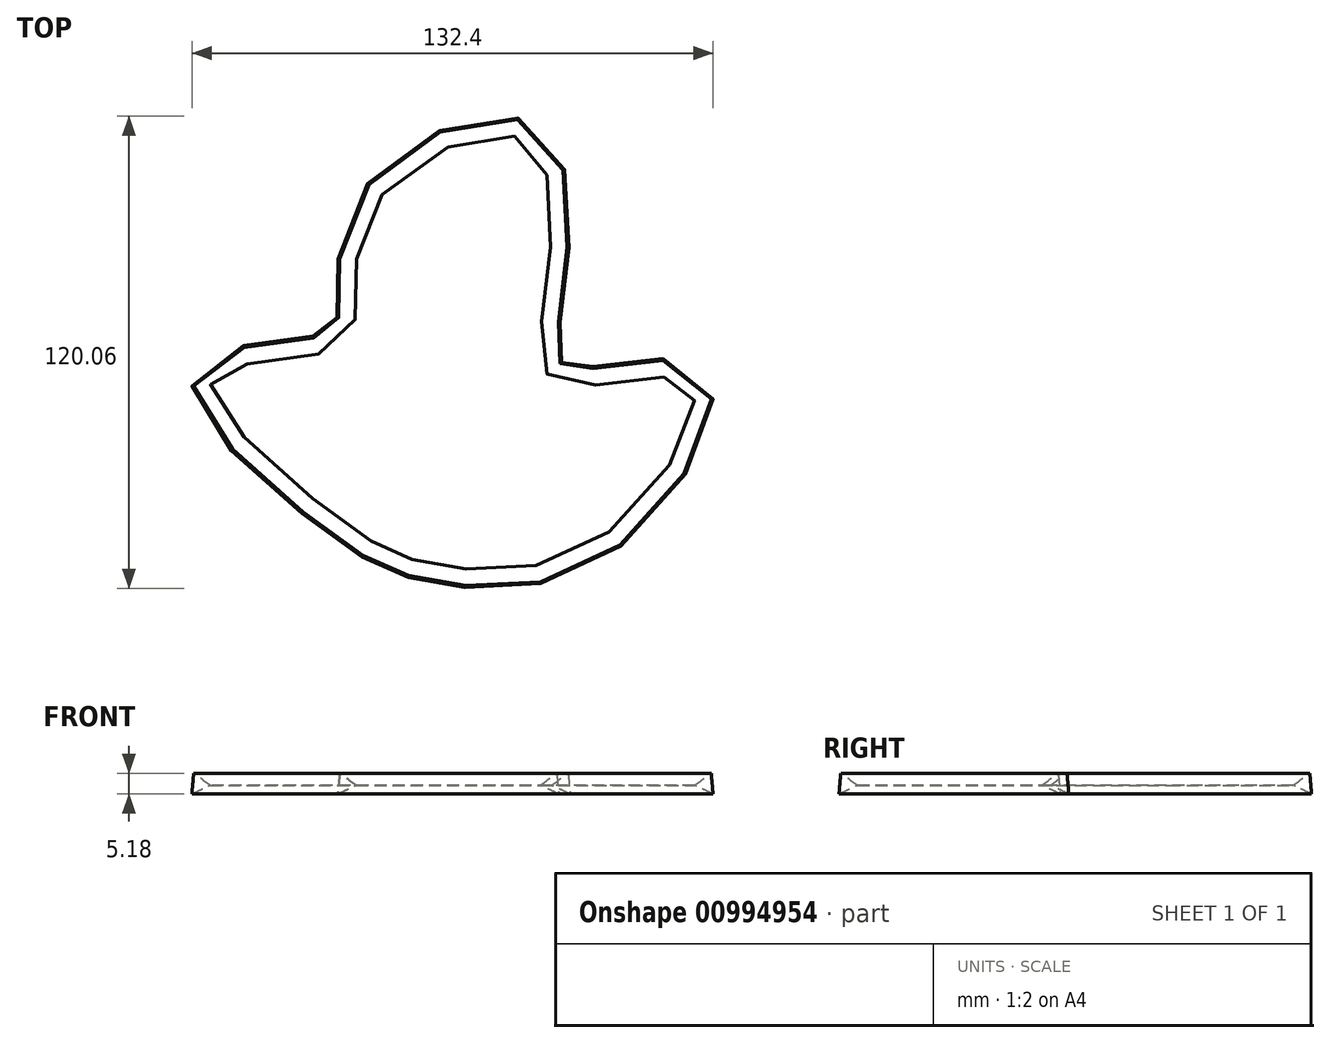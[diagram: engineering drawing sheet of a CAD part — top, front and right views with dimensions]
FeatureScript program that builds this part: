
annotation { "Feature Type Name" : "Feature", "Feature Type Description" : "" }
export const myFeature = defineFeature(function(context is Context, id is Id, definition is map)
    precondition{}
    {
        {
            var Q0;
            Q0=qCreatedBy(makeId("Front.planeOp"),FACE);
            var sketch = newSketch(context, id + "F0", { "sketchPlane" : qUnion([Q0])});
            skCircle(sketch, "E0.cCircle", {"center": v(-5.22, 0) * mm, "radius": 1.5 * mm, "construction": true});
            skLineSegment(sketch, "E0.0", {"start": v(-2.23, -0.26) * mm, "end": v(-6.94, -2.46) * mm});
            skLineSegment(sketch, "E0.1", {"start": v(-6.94, -2.46) * mm, "end": v(-6.5, 2.72) * mm});
            skLineSegment(sketch, "E0.2", {"start": v(-6.5, 2.72) * mm, "end": v(-2.23, -0.26) * mm});
            skPoint(sketch, "E0.0.midPoint", {"position": v(-4.59, -1.36) * mm});
            skSolve(sketch);
        }
        {
            var Q0;
            Q0=qCreatedBy(makeId("Top.planeOp"),FACE);
            var sketch = newSketch(context, id + "F1", { "sketchPlane" : qUnion([Q0])});
            skFitSpline(sketch, "E1", {"points": [v(-5.28, -67.45) * mm, v(-39.28, -30.08) * mm, v(-6.1, -21.25) * mm, v(-0.53, 9.49) * mm, v(39.65, 30.97) * mm, v(46.47, -6.02) * mm, v(49.5, -31.26) * mm, v(82.37, -31.44) * mm, v(59.82, -71.38) * mm, v(15.85, -77.6) * mm, v(-5.28, -67.45) * mm]});
            skSolve(sketch);
        }
        {
            var Q0;
            Q0=makeQuery(id+"F0.imprint","IMPRINT",FACE,{"disambiguationData":[TD([[makeQuery(id+"F0.imprint","IMPRINT",EDGE,{"derivedFrom":sQuery(id+"F0.wireOp",EDGE,"E0.0")}),-1.0]])]});
            var Q1;
            Q1=sQuery(id+"F1.wireOp",EDGE,"E1");
            sweep(context, id + "F2", {"profiles" : qUnion([Q0]), "path" : qUnion([Q1])});
        }
    });
